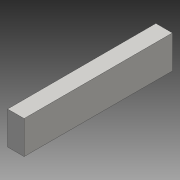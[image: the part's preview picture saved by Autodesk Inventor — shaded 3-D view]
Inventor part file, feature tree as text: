
AUTODESK INVENTOR PART (.ipt)
format: ipt  version: 2016 (Build 200138000, 138)  size: 69,120 bytes
history: native  units: mm
features: extrude x1, sketch x1
ambient origin geometry x8: Origin, YZ Plane, XZ Plane, XY Plane, X Axis, Y Axis, Z Axis, Center Point
bodies: 实体1 (feature_tree)
feature tree (2):
  extrude  "拉伸1"  Depth=20.0mm
  sketch  "草图1"  dims[d0=40.0mm d1=20.0mm d2=180.0mm d3=0.0mm]
